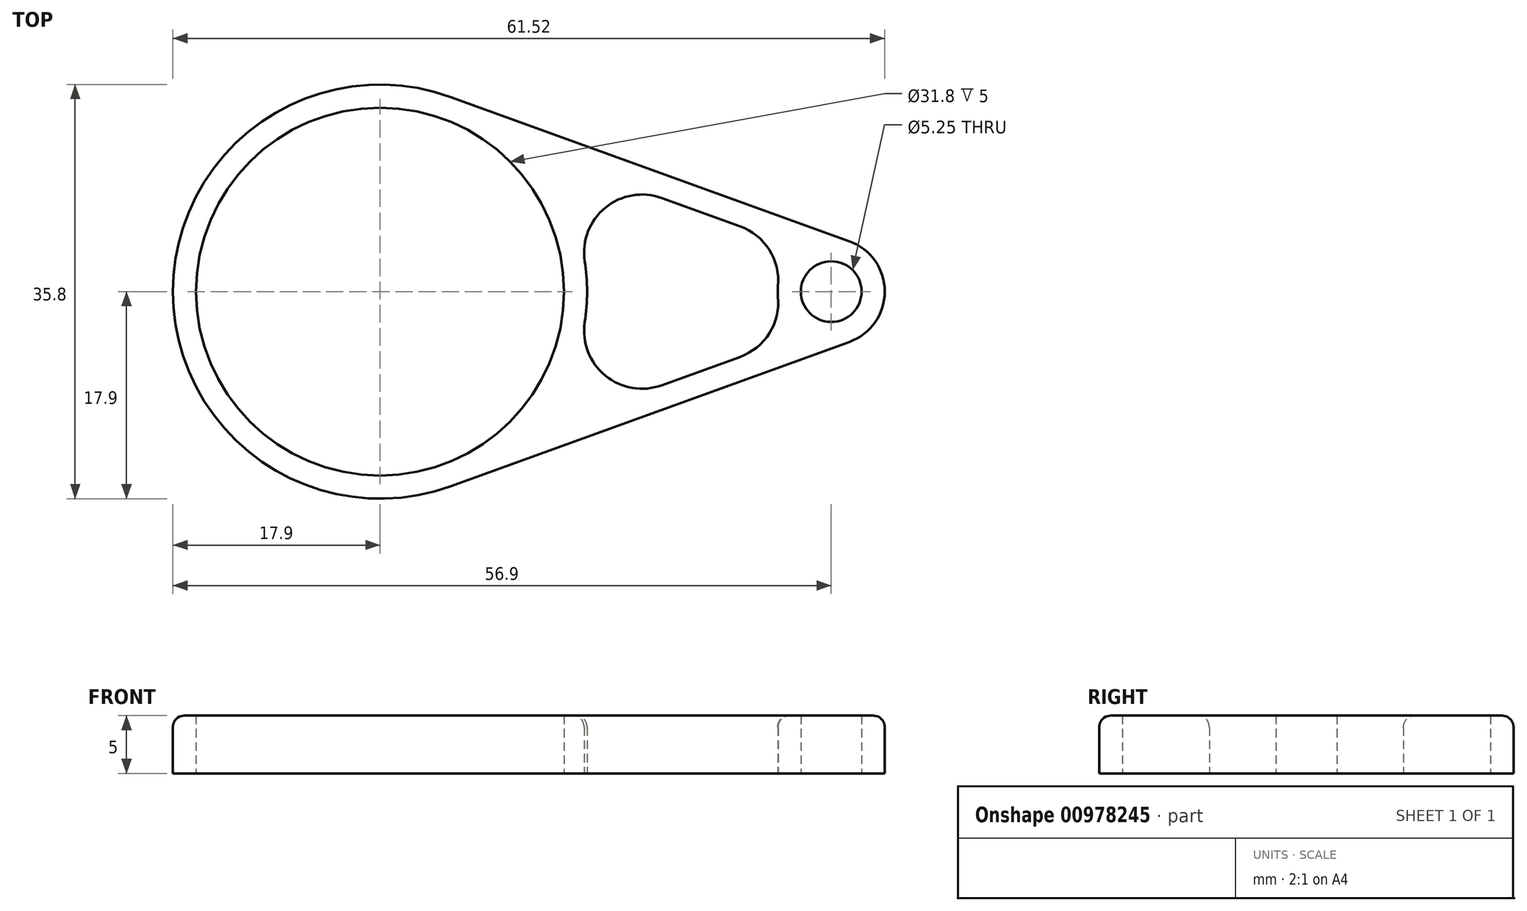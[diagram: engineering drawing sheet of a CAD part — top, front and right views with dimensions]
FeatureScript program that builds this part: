
annotation { "Feature Type Name" : "Feature", "Feature Type Description" : "" }
export const myFeature = defineFeature(function(context is Context, id is Id, definition is map)
    precondition{}
    {
        {
            var Q0;
            Q0=qCreatedBy(makeId("Top.planeOp"),FACE);
            var sketch = newSketch(context, id + "F0", { "sketchPlane" : qUnion([Q0])});
            skCircle(sketch, "E0", {"center": v(0, 0) * mm, "radius": 15.9 * mm});
            skLineSegment(sketch, "E1", {"start": v(0, 0) * mm, "end": v(39, 0) * mm, "construction": true});
            skCircle(sketch, "E2", {"center": v(39, 0) * mm, "radius": 2.62 * mm});
            skLineSegment(sketch, "E3", {"start": v(5.41, 14.95) * mm, "end": v(39.9, 2.47) * mm});
            skLineSegment(sketch, "E4", {"start": v(-34.75, 0) * mm, "end": v(54.57, 0) * mm, "construction": true});
            skLineSegment(sketch, "E5.MirrorCS", {"start": v(5.41, -14.95) * mm, "end": v(39.9, -2.47) * mm});
            skLineSegment(sketch, "E6.0", {"start": v(6.1, 16.83) * mm, "end": v(40.57, 4.35) * mm});
            skLineSegment(sketch, "E7.0", {"start": v(6.1, -16.83) * mm, "end": v(40.57, -4.35) * mm});
            skCircle(sketch, "E8", {"center": v(0, 0) * mm, "radius": 17.9 * mm});
            skCircle(sketch, "E9", {"center": v(39, 0) * mm, "radius": 4.63 * mm});
            skSolve(sketch);
        }
        {
            var Q0;
            {var subQ2=sQuery(id+"F0.wireOp",EDGE,"E3");var subQ5=sQuery(id+"F0.wireOp",EDGE,"E0");var subQ8=makeQuery(id+"F0.imprint","INTERSECT",VERTEX,{"derivedFrom":[subQ5,subQ2]});Q0=makeQuery(id+"F0.imprint","IMPRINT",FACE,{"disambiguationData":[TD([[makeQuery(id+"F0.imprint","IMPRINT",EDGE,{"disambiguationData":[TD([[subQ8,-1.0]])],"derivedFrom":subQ5}),-1.0]])]});}
            var Q1;
            {var subQ5=sQuery(id+"F0.wireOp",EDGE,"E6.0");Q1=makeQuery(id+"F0.imprint","IMPRINT",FACE,{"disambiguationData":[TD([[makeQuery(id+"F0.imprint","IMPRINT",EDGE,{"derivedFrom":subQ5}),-1.0]])]});}
            var Q2;
            {var subQ5=sQuery(id+"F0.wireOp",EDGE,"E7.0");Q2=makeQuery(id+"F0.imprint","IMPRINT",FACE,{"disambiguationData":[TD([[makeQuery(id+"F0.imprint","IMPRINT",EDGE,{"derivedFrom":subQ5}),1.0]])]});}
            var Q3;
            {var subQ1=sQuery(id+"F0.wireOp",EDGE,"E2");var subQ6=sQuery(id+"F0.wireOp",EDGE,"E3");var subQ8=makeQuery(id+"F0.imprint","INTERSECT",VERTEX,{"derivedFrom":[subQ1,subQ6]});Q3=makeQuery(id+"F0.imprint","IMPRINT",FACE,{"disambiguationData":[TD([[makeQuery(id+"F0.imprint","IMPRINT",EDGE,{"disambiguationData":[TD([[subQ8,1.0]])],"derivedFrom":subQ1}),-1.0]])]});}
            var Q4;
            {var subQ0=sQuery(id+"F0.wireOp",EDGE,"E3");var subQ1=sQuery(id+"F0.wireOp",EDGE,"E2");var subQ2=makeQuery(id+"F0.imprint","INTERSECT",VERTEX,{"derivedFrom":[subQ1,subQ0]});Q4=makeQuery(id+"F0.imprint","IMPRINT",FACE,{"disambiguationData":[TD([[makeQuery(id+"F0.imprint","IMPRINT",EDGE,{"disambiguationData":[TD([[subQ2,-1.0]])],"derivedFrom":subQ1}),-1.0]])]});}
            var Q5;
            {var subQ0=sQuery(id+"F0.wireOp",EDGE,"E3");var subQ1=sQuery(id+"F0.wireOp",EDGE,"E0");var subQ2=makeQuery(id+"F0.imprint","INTERSECT",VERTEX,{"derivedFrom":[subQ1,subQ0]});Q5=makeQuery(id+"F0.imprint","IMPRINT",FACE,{"disambiguationData":[TD([[makeQuery(id+"F0.imprint","IMPRINT",EDGE,{"disambiguationData":[TD([[subQ2,1.0]])],"derivedFrom":subQ1}),-1.0]])]});}
            extrude(context, id + "F1", {"entities" : qUnion([Q0, Q1, Q2, Q3, Q4, Q5]), "depth" : 5 * mm, "offsetDistance" : 25 * mm});
        }
        {
            var Q0;
            Q0=makeQuery(id+"F1.opExtrude","SWEPT_EDGE",EDGE,{"disambiguationData":[OSD([sQuery(id+"F0.wireOp",EDGE,"E3"),sQuery(id+"F0.wireOp",EDGE,"E9")])]});
            var Q1;
            Q1=makeQuery(id+"F1.opExtrude","SWEPT_EDGE",EDGE,{"disambiguationData":[OSD([sQuery(id+"F0.wireOp",EDGE,"E5.MirrorCS"),sQuery(id+"F0.wireOp",EDGE,"E9")])]});
            var Q2;
            Q2=makeQuery(id+"F1.opExtrude","SWEPT_EDGE",EDGE,{"disambiguationData":[OSD([sQuery(id+"F0.wireOp",EDGE,"E3"),sQuery(id+"F0.wireOp",EDGE,"E8")])]});
            var Q3;
            Q3=makeQuery(id+"F1.opExtrude","SWEPT_EDGE",EDGE,{"disambiguationData":[OSD([sQuery(id+"F0.wireOp",EDGE,"E5.MirrorCS"),sQuery(id+"F0.wireOp",EDGE,"E8")])]});
            fillet(context, id + "F2", {"entities" : qUnion([Q0, Q1, Q2, Q3]), "radius" : 5 * mm, "tangentPropagation" : true, "allowEdgeOverflow" : false});
        }
        {
            var Q0;
            Q0=makeQuery(id+"F1.opExtrude","CAP_EDGE",EDGE,{"disambiguationData":[OSD([sQuery(id+"F0.wireOp",EDGE,"E6.0")])],"isStart":false});
            var Q1;
            {var subQ0=sQuery(id+"F0.wireOp",EDGE,"E8");var subQ1=sQuery(id+"F0.wireOp",EDGE,"E3");Q1=makeQuery(id+"F2.opFillet","BLEND_EDGE",EDGE,{"blendedFrom":[makeQuery(id+"F1.opExtrude","SWEPT_EDGE",EDGE,{"disambiguationData":[OSD([subQ1,subQ0])]}),makeQuery(id+"F1.opExtrude","CAP_FACE",FACE,{"disambiguationData":[OSD([sQuery(id+"F0.wireOp",EDGE,"E0"),sQuery(id+"F0.wireOp",EDGE,"E2"),subQ1,sQuery(id+"F0.wireOp",EDGE,"E5.MirrorCS"),sQuery(id+"F0.wireOp",EDGE,"E6.0"),sQuery(id+"F0.wireOp",EDGE,"E7.0"),subQ0,sQuery(id+"F0.wireOp",EDGE,"E9")])],"isStart":false})],"blendedInto":[makeQuery(id+"F1.opExtrude","CAP_FACE",FACE,{"disambiguationData":[OSD([sQuery(id+"F0.wireOp",EDGE,"E0"),sQuery(id+"F0.wireOp",EDGE,"E2"),subQ1,sQuery(id+"F0.wireOp",EDGE,"E5.MirrorCS"),sQuery(id+"F0.wireOp",EDGE,"E6.0"),sQuery(id+"F0.wireOp",EDGE,"E7.0"),subQ0,sQuery(id+"F0.wireOp",EDGE,"E9")])],"isStart":false})]});}
            fillet(context, id + "F3", {"entities" : qUnion([Q0, Q1]), "radius" : 1 * mm, "tangentPropagation" : true, "allowEdgeOverflow" : false});
        }
    });
